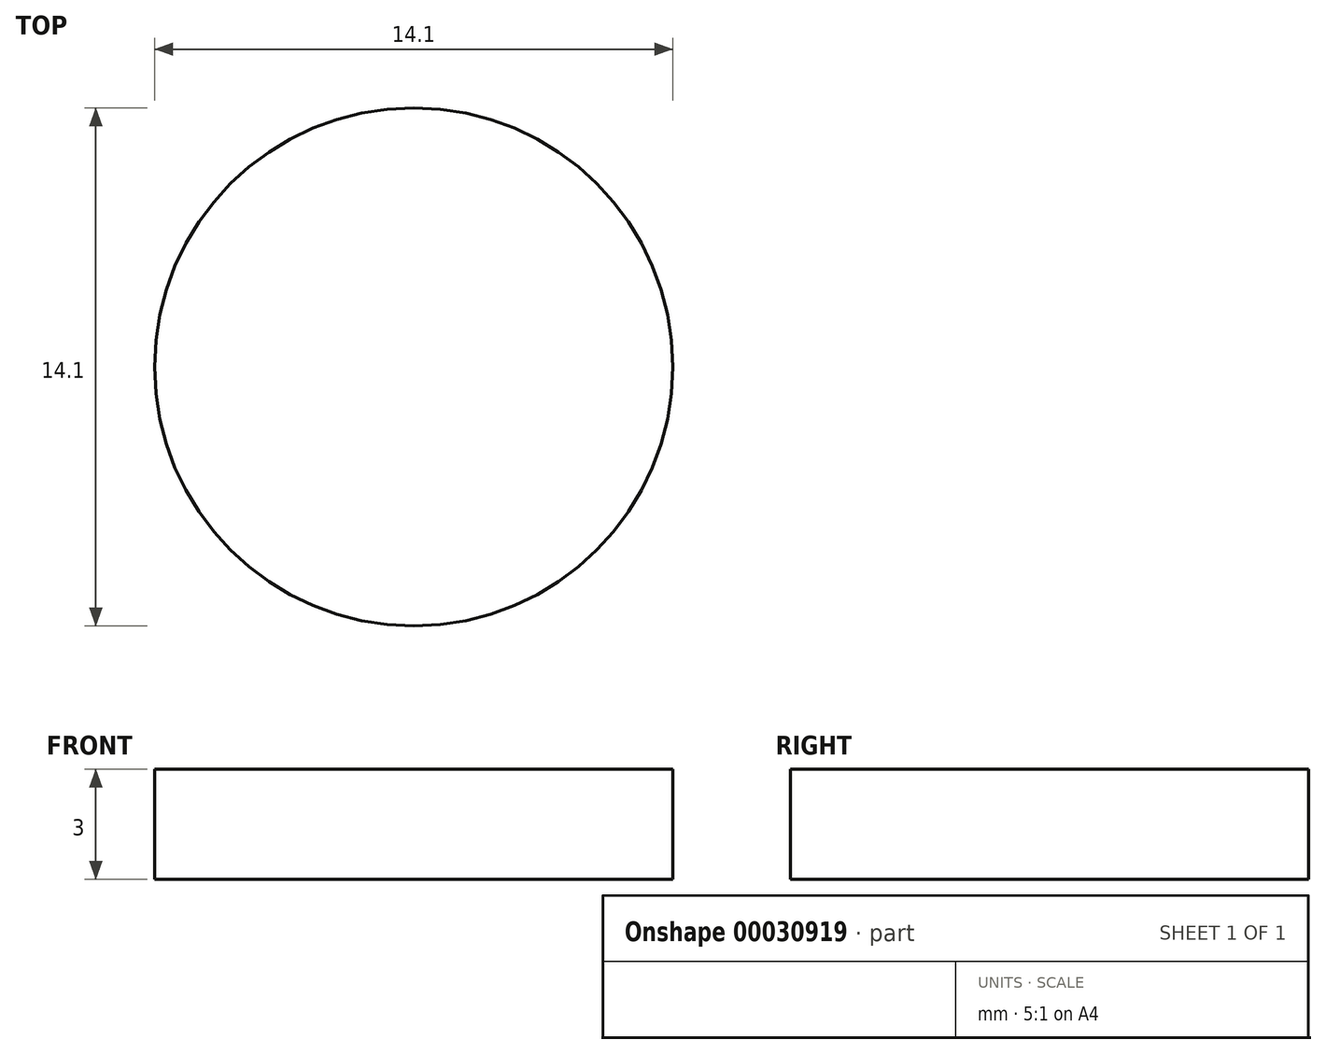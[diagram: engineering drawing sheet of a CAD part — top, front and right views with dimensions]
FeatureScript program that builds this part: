
annotation { "Feature Type Name" : "Feature", "Feature Type Description" : "" }
export const myFeature = defineFeature(function(context is Context, id is Id, definition is map)
    precondition{}
    {
        {
            var Q0;
            Q0=qCreatedBy(makeId("Top.planeOp"),FACE);
            var sketch = newSketch(context, id + "F0", { "sketchPlane" : qUnion([Q0])});
            skCircle(sketch, "E0", {"center": v(0, 0) * mm, "radius": 7.05 * mm});
            skSolve(sketch);
        }
        {
            var Q0;
            Q0 = qSketchRegion(id + "F0", true);
            extrude(context, id + "F1", {"entities" : qUnion([Q0]), "depth" : 3 * mm});
        }
    });
